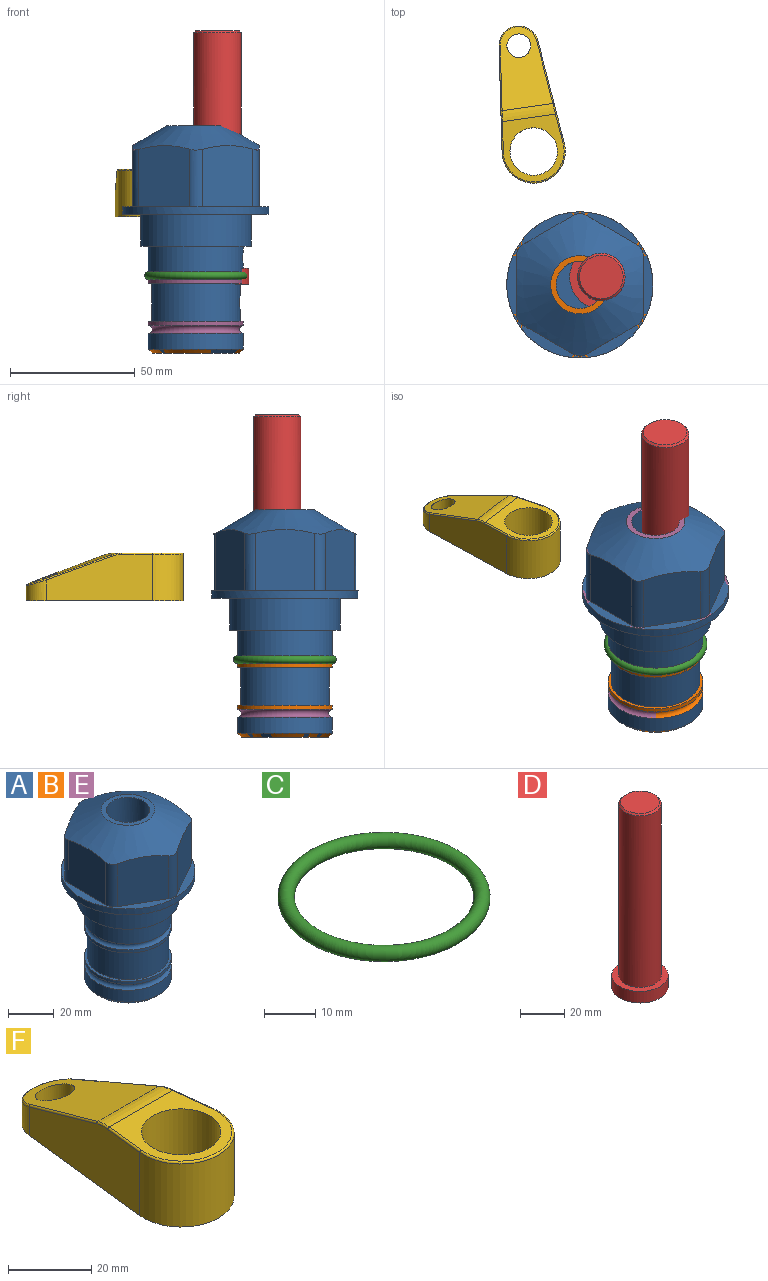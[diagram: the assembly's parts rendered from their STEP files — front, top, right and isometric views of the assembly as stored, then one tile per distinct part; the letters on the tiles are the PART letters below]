
ASSEMBLY  parts=6 mates=1
PART A: 36 faces, bbox 58.7x58.7x91.2 mm
  f0: cylinder r=17.78mm len=35.56mm, axis (0,0,1), area 1670.8mm2, adj f23,f24,f31
  f1: cylinder r=19.05mm len=38.1mm, axis (0,0,1), area 1191.9mm2, adj f26,f27,f30
  f2: plane 58.66x58.66mm, normal (0,0,-1), area 1150.6mm2, adj f3,f28
  f3: cylinder r=29.33mm len=58.66mm, axis (0,0,-1), area 585.1mm2, adj f2,f4
  f4: plane 58.66x58.66mm, normal (0,0,1), area 475.9mm2, adj f3,f5,f6,f7,f8,f9,f10,f11
  f5: plane 24.5x20.32mm, normal (-0.5,0.87,0), area 562.8mm2, adj f4,f15,f16,f17
  f6: plane 24.5x20.32mm, normal (0.5,0.87,0), area 562.8mm2, adj f4,f14,f15,f17
  f7: plane 24.5x23.48mm, normal (1,0,0), area 562.8mm2, adj f4,f13,f14,f17
  f8: plane 24.5x20.32mm, normal (0.5,-0.87,0), area 562.8mm2, adj f4,f12,f13,f17
  f9: plane 24.5x20.32mm, normal (-0.5,-0.87,0), area 562.8mm2, adj f4,f11,f12,f17
  f10: plane 24.5x23.48mm, normal (-1,0,0), area 562.8mm2, adj f4,f11,f16,f17
  f11: cylinder r=5.08mm len=23.01mm, axis (0,0,-1), area 121.2mm2, adj f4,f9,f10,f17
  f12: cylinder r=5.08mm len=23.01mm, axis (0,0,-1), area 121.2mm2, adj f4,f8,f9,f17
  f13: cylinder r=5.08mm len=23.01mm, axis (0,0,-1), area 121.2mm2, adj f4,f7,f8,f17
  f14: cylinder r=5.08mm len=23.01mm, axis (0,0,-1), area 121.2mm2, adj f4,f6,f7,f17
  f15: cylinder r=5.08mm len=23.01mm, axis (0,0,-1), area 121.2mm2, adj f4,f5,f6,f17
  f16: cylinder r=5.08mm len=23.01mm, axis (0,0,-1), area 121.2mm2, adj f4,f5,f10,f17
  f17: cone r=11.73mm half-angle=60deg, axis (0,0,-1), area 2071.8mm2, adj f5,f6,f7,f8,f9,f10,f11,f12
  f18: plane 23.46x23.46mm, normal (0,0,1), area 147.4mm2, adj f17,f35
  f19: plane 34.93x34.93mm, normal (0,0,-1), area 958mm2, adj f29
  f20: cylinder r=19.05mm len=38.1mm, axis (0,0,1), area 760.1mm2, adj f21,f29
  f21: torus R=19.05mm, axis (0,0,1), area 565.3mm2, adj f20,f22
  f22: cylinder r=19.05mm len=38.1mm, axis (0,0,1), area 190mm2, adj f21,f23
  f23: plane 38.1x38.1mm, normal (0,0,1), area 146.9mm2, adj f0,f22
  f24: plane 38.1x38.1mm, normal (0,0,-1), area 146.9mm2, adj f0,f25
  f25: cylinder r=19.05mm len=38.1mm, axis (0,0,1), area 190mm2, adj f24,f26
  f26: torus R=19.05mm, axis (0,0,1), area 565.3mm2, adj f1,f25
  f27: plane 44.45x44.45mm, normal (0,0,-1), area 411.7mm2, adj f1,f28
  f28: cylinder r=22.23mm len=44.45mm, axis (0,0,1), area 1773.5mm2, adj f2,f27
  f29: cone r=19.05mm half-angle=45deg, axis (0,0,1), area 257.5mm2, adj f19,f20
  f30: cylinder r=3.17mm len=6.75mm, axis (-1,0,0), area 128mm2, adj f1,f33
  f31: cylinder r=3.17mm len=6.35mm, axis (-1,0,0), area 102.5mm2, adj f0,f33
  f32: plane 25.4x25.4mm, normal (0,0,1), area 506.7mm2, adj f33
  f33: cylinder r=12.7mm len=66.42mm, axis (0,0,-1), area 5236.2mm2, adj f30,f31,f32,f34
  f34: cone r=9.53mm half-angle=30deg, axis (0,0,-1), area 443.4mm2, adj f33,f35
  f35: cylinder r=9.53mm len=19.05mm, axis (0,0,-1), area 849mm2, adj f18,f34
PART B: same geometry as A
PART C: 1 faces, bbox 44.7x44.7x3.2 mm
  f0: torus R=19.05mm, axis (0,0,1), area 1193.9mm2
PART D: 6 faces, bbox 25.4x25.4x101.6 mm
  f0: plane 17.46x17.46mm, normal (0,0,1), area 239.5mm2, adj f5
  f1: plane 25.4x25.4mm, normal (0,0,-1), area 506.7mm2, adj f2
  f2: cylinder r=12.7mm len=25.4mm, axis (0,0,1), area 506.7mm2, adj f1,f3
  f3: plane 25.4x25.4mm, normal (0,0,1), area 221.7mm2, adj f2,f4
  f4: cylinder r=9.53mm len=94.46mm, axis (0,0,1), area 5653mm2, adj f3,f5
  f5: cone r=8.73mm half-angle=45deg, axis (0,0,-1), area 64.4mm2, adj f0,f4
PART E: same geometry as A
PART F: 44 faces, bbox 27.5x64.5x19.1 mm
  f0: plane 2.3x0.95mm, normal (0,0,-1), area 1mm2, adj f25,f30,f34
  f1: plane 63.5x25.4mm, normal (0,0,-1), area 561.7mm2, adj f2,f3,f4,f5,f6,f7,f19,f20
  f2: cylinder r=12.7mm len=25.4mm, axis (0,0,-1), area 792.2mm2, adj f1,f3,f5,f13
  f3: plane 42.33x18.54mm, normal (0.99,0.11,0), area 647mm2, adj f1,f2,f4,f11,f12,f14
  f4: cylinder r=7.94mm len=15.78mm, axis (0,0,-1), area 158.6mm2, adj f1,f3,f5,f16
  f5: plane 42.33x18.54mm, normal (-0.99,0.11,0), area 647mm2, adj f1,f2,f4,f15,f17,f18
  f6: cylinder r=9.53mm len=19.05mm, axis (0,0,-1), area 1140.1mm2, adj f1,f8
  f7: cylinder r=4.76mm len=10.98mm, axis (0,0,-1), area 276.1mm2, adj f1,f9
  f8: plane 25.83x24.38mm, normal (0,0,1), area 262.2mm2, adj f6,f10,f11,f13,f15
  f9: plane 32.49x20.55mm, normal (0,0.34,0.94), area 489.9mm2, adj f7,f10,f14,f16,f18
  f10: cylinder r=12.7mm len=21.49mm, axis (-1,0,0), area 93.2mm2, adj f8,f9,f12,f17
  f11: cylinder r=0.51mm len=12.34mm, axis (0.11,-0.99,0), area 9.9mm2, adj f3,f8,f12,f13
  f12: bspline ~7.62x1.64mm, area 3.5mm2, adj f3,f10,f11,f14
  f13: torus R=12.19mm, axis (0,0,1), area 33.6mm2, adj f2,f8,f11,f15
  f14: cylinder r=0.51mm len=26.01mm, axis (0.1,-0.93,0.34), area 21.6mm2, adj f3,f9,f12,f16
  f15: cylinder r=0.51mm len=12.34mm, axis (0.11,0.99,0), area 9.9mm2, adj f5,f8,f13,f17
  f16: bspline ~15.78x7.05mm, area 15.7mm2, adj f4,f9,f14,f18
  f17: bspline ~7.62x1.64mm, area 3.5mm2, adj f5,f10,f15,f18
  f18: cylinder r=0.51mm len=26.01mm, axis (0.1,0.93,-0.34), area 21.6mm2, adj f5,f9,f16,f17
  f19: plane 21.6x14.29mm, normal (-0.99,-0.11,0), area 242.6mm2, adj f1,f26,f28,f34,f36,f38
  f20: plane 21.6x14.29mm, normal (0.99,-0.11,0), area 242.6mm2, adj f1,f27,f29,f37,f39,f41
  f21: cylinder r=12.7mm len=14.29mm, axis (0,0,-1), area 173.2mm2, adj f1,f26,f27,f30,f31,f33
  f22: cylinder r=7.94mm len=7.63mm, axis (0,0,-1), area 53.8mm2, adj f1,f28,f29,f42
  f23: plane 2.3x0.95mm, normal (0,0,-1), area 1mm2, adj f25,f33,f37
  f24: plane 17.94x12.32mm, normal (0,-0.34,-0.94), area 191.2mm2, adj f25,f38,f41,f42
  f25: cylinder r=9.53mm len=12.93mm, axis (-1,0,0), area 37.5mm2, adj f0,f23,f24,f31,f36,f39
  f26: cylinder r=1.59mm len=14.29mm, axis (0,0,-1), area 49mm2, adj f1,f19,f21,f32
  f27: cylinder r=1.59mm len=14.29mm, axis (0,0,-1), area 49mm2, adj f1,f20,f21,f35
  f28: cylinder r=1.59mm len=7.28mm, axis (0,0,-1), area 22.1mm2, adj f1,f19,f22,f40
  f29: cylinder r=1.59mm len=7.28mm, axis (0,0,-1), area 22.1mm2, adj f1,f20,f22,f43
  f30: torus R=14.29mm, axis (0,0,1), area 5.8mm2, adj f0,f21,f31,f32
  f31: bspline ~11.06x2.73mm, area 20.8mm2, adj f21,f25,f30,f33
  f32: sphere r=1.59mm, area 5.4mm2, adj f26,f30,f34
  f33: torus R=14.29mm, axis (0,0,1), area 5.8mm2, adj f21,f23,f31,f35
  f34: cylinder r=1.59mm len=1.68mm, axis (-0.11,0.99,0), area 2.4mm2, adj f0,f19,f32,f36
  f35: sphere r=1.59mm, area 5.4mm2, adj f27,f33,f37
  f36: bspline ~5.82x2.33mm, area 7.7mm2, adj f19,f25,f34,f38
  f37: cylinder r=1.59mm len=1.68mm, axis (0.11,0.99,0), area 2.4mm2, adj f20,f23,f35,f39
  f38: cylinder r=1.59mm len=18.33mm, axis (0.1,-0.93,0.34), area 46.7mm2, adj f19,f24,f36,f40
  f39: bspline ~5.82x2.33mm, area 7.7mm2, adj f20,f25,f37,f41
  f40: sphere r=1.59mm, area 3.6mm2, adj f28,f38,f42
  f41: cylinder r=1.59mm len=18.33mm, axis (0.1,0.93,-0.34), area 46.7mm2, adj f20,f24,f39,f43
  f42: bspline ~8.31x1.84mm, area 15.3mm2, adj f22,f24,f40,f43
  f43: sphere r=1.59mm, area 3.6mm2, adj f29,f41,f42
PLACE A at identity
PLACE B at identity
PLACE C at identity
PLACE D rot(axis=(0,0,1),8deg) t=(8.61,3.09,0)mm
PLACE E at identity
PLACE F rot(axis=(0,0,1),8deg) t=(-18.53,53.5,-0.91)mm
MATE cylindrical D.f2 <-> F.f2  axis (0,0,1) through (8.61,3.09,73.66)mm
